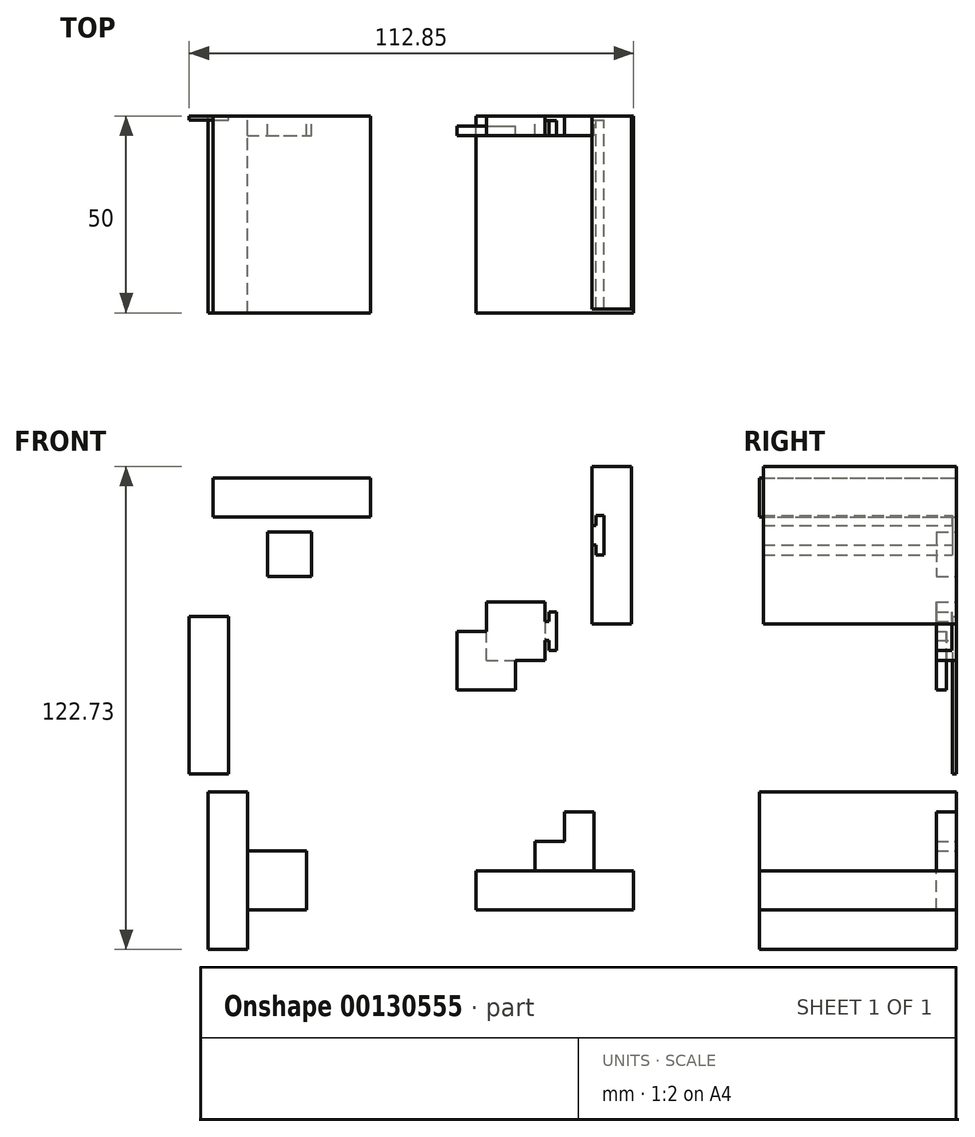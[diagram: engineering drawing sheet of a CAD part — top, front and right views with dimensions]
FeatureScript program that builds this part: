
annotation { "Feature Type Name" : "Feature", "Feature Type Description" : "" }
export const myFeature = defineFeature(function(context is Context, id is Id, definition is map)
    precondition{}
    {
        {
            var Q0;
            Q0=qCreatedBy(makeId("Front.planeOp"),FACE);
            var sketch = newSketch(context, id + "F0", { "sketchPlane" : qUnion([Q0])});
            skLineSegment(sketch, "E0", {"start": v(-53.3, -18.29) * mm, "end": v(-53.3, -58.29) * mm});
            skLineSegment(sketch, "E1", {"start": v(-53.3, -58.29) * mm, "end": v(-43.3, -58.29) * mm});
            skLineSegment(sketch, "E2", {"start": v(-43.3, -58.29) * mm, "end": v(-43.3, -48.29) * mm});
            skLineSegment(sketch, "E3", {"start": v(-43.3, -48.29) * mm, "end": v(-53.3, -48.29) * mm});
            skLineSegment(sketch, "E4", {"start": v(-43.3, -48.29) * mm, "end": v(-43.3, -18.29) * mm});
            skLineSegment(sketch, "E5", {"start": v(-53.3, -18.29) * mm, "end": v(-43.3, -18.29) * mm});
            skLineSegment(sketch, "E6", {"start": v(14.75, -48.29) * mm, "end": v(54.75, -48.29) * mm});
            skLineSegment(sketch, "E7", {"start": v(54.75, -48.29) * mm, "end": v(54.75, -38.29) * mm});
            skLineSegment(sketch, "E8", {"start": v(54.75, -38.29) * mm, "end": v(44.75, -38.29) * mm});
            skLineSegment(sketch, "E9", {"start": v(44.75, -38.29) * mm, "end": v(44.75, -48.29) * mm});
            skLineSegment(sketch, "E10", {"start": v(44.75, -38.29) * mm, "end": v(14.75, -38.29) * mm});
            skLineSegment(sketch, "E11", {"start": v(14.75, -38.29) * mm, "end": v(14.75, -48.29) * mm});
            skLineSegment(sketch, "E12", {"start": v(54.25, 64.44) * mm, "end": v(54.25, 24.44) * mm});
            skLineSegment(sketch, "E13", {"start": v(54.25, 64.44) * mm, "end": v(44.25, 64.44) * mm});
            skLineSegment(sketch, "E14", {"start": v(44.25, 64.44) * mm, "end": v(44.25, 54.44) * mm});
            skLineSegment(sketch, "E15", {"start": v(44.25, 54.44) * mm, "end": v(54.25, 54.44) * mm});
            skLineSegment(sketch, "E16", {"start": v(44.25, 24.44) * mm, "end": v(54.25, 24.44) * mm});
            skLineSegment(sketch, "E17", {"start": v(-52, 61.52) * mm, "end": v(-12, 61.52) * mm});
            skLineSegment(sketch, "E18", {"start": v(-52, 61.52) * mm, "end": v(-52, 51.52) * mm});
            skLineSegment(sketch, "E19", {"start": v(-52, 51.52) * mm, "end": v(-42, 51.52) * mm});
            skLineSegment(sketch, "E20", {"start": v(-42, 51.52) * mm, "end": v(-42, 61.52) * mm});
            skLineSegment(sketch, "E21", {"start": v(-42, 51.52) * mm, "end": v(-12, 51.52) * mm});
            skLineSegment(sketch, "E22", {"start": v(-12, 51.52) * mm, "end": v(-12, 61.52) * mm});
            skLineSegment(sketch, "E23", {"start": v(-42, 51.52) * mm, "end": v(-27, 51.52) * mm});
            skLineSegment(sketch, "E24", {"start": v(-43.3, -48.29) * mm, "end": v(-28.3, -48.29) * mm});
            skLineSegment(sketch, "E25", {"start": v(-28.3, -48.29) * mm, "end": v(-28.3, -33.29) * mm});
            skLineSegment(sketch, "E26", {"start": v(-28.3, -33.29) * mm, "end": v(-43.3, -33.29) * mm});
            skLineSegment(sketch, "E27", {"start": v(-42, 51.52) * mm, "end": v(-42, 36.52) * mm});
            skLineSegment(sketch, "E28", {"start": v(-42, 36.52) * mm, "end": v(-27, 36.52) * mm});
            skLineSegment(sketch, "E29", {"start": v(-27, 51.52) * mm, "end": v(-27, 36.52) * mm});
            skLineSegment(sketch, "E30", {"start": v(-27, 36.52) * mm, "end": v(-38.25, 36.52) * mm});
            skLineSegment(sketch, "E31", {"start": v(-38.25, 36.52) * mm, "end": v(-38.25, 47.77) * mm});
            skLineSegment(sketch, "E32", {"start": v(-38.25, 47.77) * mm, "end": v(-27, 47.77) * mm});
            skLineSegment(sketch, "E33", {"start": v(-34.5, 36.52) * mm, "end": v(-34.5, 44.02) * mm});
            skLineSegment(sketch, "E34", {"start": v(-34.5, 44.02) * mm, "end": v(-27, 44.02) * mm});
            skLineSegment(sketch, "E35", {"start": v(-34.5, 44.02) * mm, "end": v(-27, 47.77) * mm});
            skLineSegment(sketch, "E36", {"start": v(-35.8, -33.29) * mm, "end": v(-35.8, -40.79) * mm});
            skLineSegment(sketch, "E37", {"start": v(-35.8, -40.79) * mm, "end": v(-28.3, -40.79) * mm});
            skLineSegment(sketch, "E38", {"start": v(44.75, -38.29) * mm, "end": v(44.75, -23.29) * mm});
            skLineSegment(sketch, "E39", {"start": v(44.75, -23.29) * mm, "end": v(29.75, -23.29) * mm});
            skLineSegment(sketch, "E40", {"start": v(29.75, -23.29) * mm, "end": v(29.75, -38.29) * mm});
            skLineSegment(sketch, "E41", {"start": v(37.25, -23.29) * mm, "end": v(37.25, -30.79) * mm});
            skLineSegment(sketch, "E42", {"start": v(37.25, -30.79) * mm, "end": v(29.75, -30.79) * mm});
            skLineSegment(sketch, "E43", {"start": v(37.25, -23.29) * mm, "end": v(44.75, -23.29) * mm});
            skLineSegment(sketch, "E44", {"start": v(41, -23.29) * mm, "end": v(41, -34.54) * mm});
            skLineSegment(sketch, "E45", {"start": v(41, -34.54) * mm, "end": v(29.75, -34.54) * mm});
            skLineSegment(sketch, "E46", {"start": v(37.25, -30.79) * mm, "end": v(41, -23.29) * mm});
            skLineSegment(sketch, "E47", {"start": v(44.25, 39.44) * mm, "end": v(44.25, 24.44) * mm});
            skLineSegment(sketch, "E48", {"start": v(44.25, 39.44) * mm, "end": v(44.25, 44.44) * mm});
            skLineSegment(sketch, "E49", {"start": v(44.25, 54.44) * mm, "end": v(44.25, 49.44) * mm});
            skLineSegment(sketch, "E50", {"start": v(44.25, 49.44) * mm, "end": v(45.25, 49.44) * mm});
            skLineSegment(sketch, "E51", {"start": v(44.25, 44.44) * mm, "end": v(45.25, 44.44) * mm});
            skLineSegment(sketch, "E52", {"start": v(45.25, 44.44) * mm, "end": v(45.25, 41.94) * mm});
            skPoint(sketch, "E52.endSnap0", {"position": v(44.25, 41.94) * mm});
            skLineSegment(sketch, "E53", {"start": v(45.25, 49.44) * mm, "end": v(45.25, 51.94) * mm});
            skPoint(sketch, "E53.endSnap0", {"position": v(44.25, 51.94) * mm});
            skLineSegment(sketch, "E54", {"start": v(45.25, 51.94) * mm, "end": v(47.25, 51.94) * mm});
            skLineSegment(sketch, "E55", {"start": v(45.25, 41.94) * mm, "end": v(47.25, 41.94) * mm});
            skLineSegment(sketch, "E56", {"start": v(47.25, 51.94) * mm, "end": v(47.25, 41.94) * mm});
            skLineSegment(sketch, "E57", {"start": v(9.93, 22.55) * mm, "end": v(9.93, 7.65) * mm});
            skLineSegment(sketch, "E58", {"start": v(9.93, 7.65) * mm, "end": v(24.83, 7.65) * mm});
            skLineSegment(sketch, "E59", {"start": v(24.83, 7.65) * mm, "end": v(24.83, 22.55) * mm});
            skLineSegment(sketch, "E60", {"start": v(9.93, 22.55) * mm, "end": v(24.83, 22.55) * mm});
            skPoint(sketch, "E61.endSnap0", {"position": v(17.38, 22.55) * mm});
            skLineSegment(sketch, "E62", {"start": v(17.38, 15.15) * mm, "end": v(32.28, 15.15) * mm});
            skLineSegment(sketch, "E63", {"start": v(17.38, 15.15) * mm, "end": v(17.38, 30.05) * mm});
            skLineSegment(sketch, "E64", {"start": v(17.38, 30.05) * mm, "end": v(32.28, 30.05) * mm});
            skLineSegment(sketch, "E65", {"start": v(44.25, 49.44) * mm, "end": v(44.25, 44.44) * mm});
            skLineSegment(sketch, "E66", {"start": v(32.28, 15.15) * mm, "end": v(32.28, 20.15) * mm});
            skLineSegment(sketch, "E67", {"start": v(32.28, 30.05) * mm, "end": v(32.28, 25.05) * mm});
            skLineSegment(sketch, "E68", {"start": v(32.28, 25.05) * mm, "end": v(33.28, 25.05) * mm});
            skLineSegment(sketch, "E69", {"start": v(33.28, 25.05) * mm, "end": v(33.28, 27.5) * mm});
            skLineSegment(sketch, "E70", {"start": v(33.28, 27.5) * mm, "end": v(35.18, 27.5) * mm});
            skLineSegment(sketch, "E71", {"start": v(32.28, 20.15) * mm, "end": v(33.28, 20.15) * mm});
            skLineSegment(sketch, "E72", {"start": v(33.28, 20.15) * mm, "end": v(33.28, 17.7) * mm});
            skLineSegment(sketch, "E73", {"start": v(33.28, 17.7) * mm, "end": v(35.18, 17.7) * mm});
            skLineSegment(sketch, "E74", {"start": v(35.18, 27.5) * mm, "end": v(35.18, 17.7) * mm});
            skLineSegment(sketch, "E75", {"start": v(32.28, 25.05) * mm, "end": v(32.28, 20.15) * mm});
            skLineSegment(sketch, "E76.bottom", {"start": v(-58.1, 26.35) * mm, "end": v(-48.1, 26.35) * mm});
            skLineSegment(sketch, "E76.top", {"start": v(-58.1, -13.65) * mm, "end": v(-48.1, -13.65) * mm});
            skLineSegment(sketch, "E76.left", {"start": v(-58.1, 26.35) * mm, "end": v(-58.1, -13.65) * mm});
            skLineSegment(sketch, "E76.right", {"start": v(-48.1, 26.35) * mm, "end": v(-48.1, -13.65) * mm});
            skSolve(sketch);
        }
        {
            var Q0;
            {var subQ0=sQuery(id+"F0.wireOp",EDGE,"E1");Q0=makeQuery(id+"F0.imprint","IMPRINT",FACE,{"disambiguationData":[TD([[makeQuery(id+"F0.imprint","IMPRINT",EDGE,{"derivedFrom":subQ0}),1.0]])]});}
            var Q1;
            {var subQ0=sQuery(id+"F0.wireOp",EDGE,"E7");Q1=makeQuery(id+"F0.imprint","IMPRINT",FACE,{"disambiguationData":[TD([[makeQuery(id+"F0.imprint","IMPRINT",EDGE,{"derivedFrom":subQ0}),1.0]])]});}
            var Q2;
            {var subQ0=sQuery(id+"F0.wireOp",EDGE,"E13");Q2=makeQuery(id+"F0.imprint","IMPRINT",FACE,{"disambiguationData":[TD([[makeQuery(id+"F0.imprint","IMPRINT",EDGE,{"derivedFrom":subQ0}),1.0]])]});}
            var Q3;
            {var subQ0=sQuery(id+"F0.wireOp",EDGE,"E18");Q3=makeQuery(id+"F0.imprint","IMPRINT",FACE,{"disambiguationData":[TD([[makeQuery(id+"F0.imprint","IMPRINT",EDGE,{"derivedFrom":subQ0}),1.0]])]});}
            var Q4;
            {var subQ4=sQuery(id+"F0.wireOp",EDGE,"E36");Q4=makeQuery(id+"F0.imprint","IMPRINT",FACE,{"disambiguationData":[TD([[makeQuery(id+"F0.imprint","IMPRINT",EDGE,{"derivedFrom":subQ4}),1.0]])]});}
            var Q5;
            Q5=makeQuery(id+"F0.imprint","IMPRINT",FACE,{"disambiguationData":[TD([[makeQuery(id+"F0.imprint","IMPRINT",EDGE,{"derivedFrom":sQuery(id+"F0.wireOp",EDGE,"E50")}),-1.0]])]});
            var Q6;
            {var subQ1=sQuery(id+"F0.wireOp",EDGE,"E57");Q6=makeQuery(id+"F0.imprint","IMPRINT",FACE,{"disambiguationData":[TD([[makeQuery(id+"F0.imprint","IMPRINT",EDGE,{"derivedFrom":subQ1}),1.0]])]});}
            var Q7;
            Q7=makeQuery(id+"F0.imprint","IMPRINT",FACE,{"disambiguationData":[TD([[makeQuery(id+"F0.imprint","IMPRINT",EDGE,{"derivedFrom":sQuery(id+"F0.wireOp",EDGE,"E68")}),-1.0]])]});
            var Q8;
            {var subQ3=sQuery(id+"F0.wireOp",EDGE,"E3");Q8=makeQuery(id+"F0.imprint","IMPRINT",FACE,{"disambiguationData":[TD([[makeQuery(id+"F0.imprint","IMPRINT",EDGE,{"derivedFrom":subQ3}),-1.0]])]});}
            var Q9;
            {var subQ1=sQuery(id+"F0.wireOp",EDGE,"E24");Q9=makeQuery(id+"F0.imprint","IMPRINT",FACE,{"disambiguationData":[TD([[makeQuery(id+"F0.imprint","IMPRINT",EDGE,{"derivedFrom":subQ1}),1.0]])]});}
            var Q10;
            {var subQ3=sQuery(id+"F0.wireOp",EDGE,"E9");Q10=makeQuery(id+"F0.imprint","IMPRINT",FACE,{"disambiguationData":[TD([[makeQuery(id+"F0.imprint","IMPRINT",EDGE,{"derivedFrom":subQ3}),-1.0]])]});}
            var Q11;
            {var subQ4=sQuery(id+"F0.wireOp",EDGE,"E38");Q11=makeQuery(id+"F0.imprint","IMPRINT",FACE,{"disambiguationData":[TD([[makeQuery(id+"F0.imprint","IMPRINT",EDGE,{"derivedFrom":subQ4}),1.0]])]});}
            var Q12;
            {var subQ2=sQuery(id+"F0.wireOp",EDGE,"E15");Q12=makeQuery(id+"F0.imprint","IMPRINT",FACE,{"disambiguationData":[TD([[makeQuery(id+"F0.imprint","IMPRINT",EDGE,{"derivedFrom":subQ2}),-1.0]])]});}
            var Q13;
            {var subQ1=sQuery(id+"F0.wireOp",EDGE,"E20");Q13=makeQuery(id+"F0.imprint","IMPRINT",FACE,{"disambiguationData":[TD([[makeQuery(id+"F0.imprint","IMPRINT",EDGE,{"derivedFrom":subQ1}),-1.0]])]});}
            var Q14;
            {var subQ1=sQuery(id+"F0.wireOp",EDGE,"E23");Q14=makeQuery(id+"F0.imprint","IMPRINT",FACE,{"disambiguationData":[TD([[makeQuery(id+"F0.imprint","IMPRINT",EDGE,{"derivedFrom":subQ1}),-1.0]])]});}
            var Q15;
            {var subQ2=sQuery(id+"F0.wireOp",EDGE,"E34");Q15=makeQuery(id+"F0.imprint","IMPRINT",FACE,{"disambiguationData":[TD([[makeQuery(id+"F0.imprint","IMPRINT",EDGE,{"derivedFrom":subQ2}),1.0]])]});}
            var Q16;
            {var subQ4=sQuery(id+"F0.wireOp",EDGE,"E33");Q16=makeQuery(id+"F0.imprint","IMPRINT",FACE,{"disambiguationData":[TD([[makeQuery(id+"F0.imprint","IMPRINT",EDGE,{"derivedFrom":subQ4}),-1.0]])]});}
            var Q17;
            {var subQ0=sQuery(id+"F0.wireOp",EDGE,"E39");Q17=makeQuery(id+"F0.imprint","IMPRINT",FACE,{"disambiguationData":[TD([[makeQuery(id+"F0.imprint","IMPRINT",EDGE,{"derivedFrom":subQ0}),1.0]])]});}
            var Q18;
            {var subQ0=sQuery(id+"F0.wireOp",EDGE,"E41");Q18=makeQuery(id+"F0.imprint","IMPRINT",FACE,{"disambiguationData":[TD([[makeQuery(id+"F0.imprint","IMPRINT",EDGE,{"derivedFrom":subQ0}),1.0]])]});}
            var Q19;
            {var subQ0=sQuery(id+"F0.wireOp",EDGE,"E60");var subQ1=sQuery(id+"F0.wireOp",EDGE,"E59");var subQ2=makeQuery(id+"F0.imprint","INTERSECT",VERTEX,{"derivedFrom":[subQ1,subQ0]});Q19=makeQuery(id+"F0.imprint","IMPRINT",FACE,{"disambiguationData":[TD([[makeQuery(id+"F0.imprint","IMPRINT",EDGE,{"disambiguationData":[TD([[subQ2,1.0]])],"derivedFrom":subQ1}),1.0]])]});}
            var Q20;
            {var subQ0=sQuery(id+"F0.wireOp",EDGE,"E64");Q20=makeQuery(id+"F0.imprint","IMPRINT",FACE,{"disambiguationData":[TD([[makeQuery(id+"F0.imprint","IMPRINT",EDGE,{"derivedFrom":subQ0}),-1.0]])]});}
            var Q21;
            {var subQ1=sQuery(id+"F0.wireOp",EDGE,"E31");Q21=makeQuery(id+"F0.imprint","IMPRINT",FACE,{"disambiguationData":[TD([[makeQuery(id+"F0.imprint","IMPRINT",EDGE,{"derivedFrom":subQ1}),-1.0]])]});}
            var Q22;
            {var subQ1=sQuery(id+"F0.wireOp",EDGE,"E42");Q22=makeQuery(id+"F0.imprint","IMPRINT",FACE,{"disambiguationData":[TD([[makeQuery(id+"F0.imprint","IMPRINT",EDGE,{"derivedFrom":subQ1}),1.0]])]});}
            extrude(context, id + "F1", {"entities" : qUnion([Q0, Q1, Q2, Q3, Q4, Q5, Q6, Q7, Q8, Q9, Q10, Q11, Q12, Q13, Q14, Q15, Q16, Q17, Q18, Q19, Q20, Q21, Q22]), "depth" : 5 * mm});
        }
        {
            var Q0;
            Q0=makeQuery(id+"F1.opExtrude","CAP_FACE",FACE,{"disambiguationData":[OSD([sQuery(id+"F0.wireOp",EDGE,"E17"),sQuery(id+"F0.wireOp",EDGE,"E18"),sQuery(id+"F0.wireOp",EDGE,"E19"),sQuery(id+"F0.wireOp",EDGE,"E21"),sQuery(id+"F0.wireOp",EDGE,"E22"),sQuery(id+"F0.wireOp",EDGE,"E27"),sQuery(id+"F0.wireOp",EDGE,"E28"),sQuery(id+"F0.wireOp",EDGE,"E29"),sQuery(id+"F0.wireOp",EDGE,"E30")])],"isStart":false});
            var sketch = newSketch(context, id + "F2", { "sketchPlane" : qUnion([Q0])});
            skLineSegment(sketch, "E77.0", {"start": v(-42, 51.52) * mm, "end": v(-42, 61.52) * mm});
            skLineSegment(sketch, "E78.0", {"start": v(-42, 51.52) * mm, "end": v(-27, 51.52) * mm});
            skLineSegment(sketch, "E79.0", {"start": v(-38.25, 47.77) * mm, "end": v(-27, 47.77) * mm});
            skLineSegment(sketch, "E80.0", {"start": v(-38.25, 36.52) * mm, "end": v(-38.25, 47.77) * mm});
            skLineSegment(sketch, "E81.0", {"start": v(-34.5, 44.02) * mm, "end": v(-27, 47.77) * mm});
            skLineSegment(sketch, "E82.0", {"start": v(-34.5, 44.02) * mm, "end": v(-27, 44.02) * mm});
            skLineSegment(sketch, "E83.0", {"start": v(-34.5, 36.52) * mm, "end": v(-34.5, 44.02) * mm});
            skLineSegment(sketch, "E84.0", {"start": v(44.25, 54.44) * mm, "end": v(54.25, 54.44) * mm});
            skLineSegment(sketch, "E85.0", {"start": v(47.25, 51.94) * mm, "end": v(47.25, 41.94) * mm});
            skLineSegment(sketch, "E86.0", {"start": v(45.25, 51.94) * mm, "end": v(47.25, 51.94) * mm});
            skLineSegment(sketch, "E87.0", {"start": v(45.25, 41.94) * mm, "end": v(47.25, 41.94) * mm});
            skLineSegment(sketch, "E88.0", {"start": v(45.25, 44.44) * mm, "end": v(45.25, 41.94) * mm});
            skLineSegment(sketch, "E89.0", {"start": v(44.25, 44.44) * mm, "end": v(45.25, 44.44) * mm});
            skLineSegment(sketch, "E90.0", {"start": v(44.25, 49.44) * mm, "end": v(45.25, 49.44) * mm});
            skLineSegment(sketch, "E91.0", {"start": v(45.25, 49.44) * mm, "end": v(45.25, 51.94) * mm});
            skLineSegment(sketch, "E92.0", {"start": v(32.28, 25.05) * mm, "end": v(32.28, 20.15) * mm});
            skLineSegment(sketch, "E93.0", {"start": v(9.93, 22.55) * mm, "end": v(24.83, 22.55) * mm});
            skLineSegment(sketch, "E94.0", {"start": v(24.83, 7.65) * mm, "end": v(24.83, 22.55) * mm});
            skLineSegment(sketch, "E95.0", {"start": v(17.38, 15.15) * mm, "end": v(32.28, 15.15) * mm});
            skLineSegment(sketch, "E96.0", {"start": v(17.38, 15.15) * mm, "end": v(17.38, 30.05) * mm});
            skLineSegment(sketch, "E97.0", {"start": v(-43.3, -48.29) * mm, "end": v(-43.3, -18.29) * mm});
            skLineSegment(sketch, "E98.0", {"start": v(-43.3, -48.29) * mm, "end": v(-53.3, -48.29) * mm});
            skLineSegment(sketch, "E99.0", {"start": v(-35.8, -33.29) * mm, "end": v(-35.8, -40.79) * mm});
            skLineSegment(sketch, "E100.0", {"start": v(-35.8, -40.79) * mm, "end": v(-28.3, -40.79) * mm});
            skLineSegment(sketch, "E101.0", {"start": v(37.25, -23.29) * mm, "end": v(37.25, -30.79) * mm});
            skLineSegment(sketch, "E102.0", {"start": v(37.25, -30.79) * mm, "end": v(29.75, -30.79) * mm});
            skLineSegment(sketch, "E103.0", {"start": v(37.25, -30.79) * mm, "end": v(41, -23.29) * mm});
            skLineSegment(sketch, "E104.0", {"start": v(41, -23.29) * mm, "end": v(41, -34.54) * mm});
            skLineSegment(sketch, "E105.0", {"start": v(41, -34.54) * mm, "end": v(29.75, -34.54) * mm});
            skLineSegment(sketch, "E106.0", {"start": v(44.75, -38.29) * mm, "end": v(14.75, -38.29) * mm});
            skLineSegment(sketch, "E107.0", {"start": v(44.75, -38.29) * mm, "end": v(44.75, -48.29) * mm});
            skSolve(sketch);
        }
        {
            var Q0;
            {var subQ0=sQuery(id+"F2.wireOp",EDGE,"E77.0");Q0=makeQuery(id+"F2.imprint","IMPRINT",FACE,{"disambiguationData":[TD([[makeQuery(id+"F2.imprint","IMPRINT",EDGE,{"derivedFrom":subQ0}),1.0]])]});}
            var Q1;
            {var subQ1=sQuery(id+"F2.wireOp",EDGE,"E77.0");Q1=makeQuery(id+"F2.imprint","IMPRINT",FACE,{"disambiguationData":[TD([[makeQuery(id+"F2.imprint","IMPRINT",EDGE,{"derivedFrom":subQ1}),-1.0]])]});}
            extrude(context, id + "F3", {"entities" : qUnion([Q0, Q1]), "operationType" : NewBodyOperationType.ADD, "depth" : 45 * mm});
        }
        {
            var Q0;
            Q0=makeQuery(id+"F1.opExtrude","CAP_FACE",FACE,{"disambiguationData":[OSD([sQuery(id+"F0.wireOp",EDGE,"E0"),sQuery(id+"F0.wireOp",EDGE,"E1"),sQuery(id+"F0.wireOp",EDGE,"E2"),sQuery(id+"F0.wireOp",EDGE,"E4"),sQuery(id+"F0.wireOp",EDGE,"E5"),sQuery(id+"F0.wireOp",EDGE,"E24"),sQuery(id+"F0.wireOp",EDGE,"E25"),sQuery(id+"F0.wireOp",EDGE,"E26")])],"isStart":false});
            var sketch = newSketch(context, id + "F4", { "sketchPlane" : qUnion([Q0])});
            skLineSegment(sketch, "E108.0", {"start": v(-43.3, -48.29) * mm, "end": v(-53.3, -48.29) * mm});
            skLineSegment(sketch, "E109.0", {"start": v(-43.3, -48.29) * mm, "end": v(-43.3, -18.29) * mm});
            skLineSegment(sketch, "E110.0", {"start": v(-35.8, -33.29) * mm, "end": v(-35.8, -40.79) * mm});
            skLineSegment(sketch, "E111.0", {"start": v(-35.8, -40.79) * mm, "end": v(-28.3, -40.79) * mm});
            skSolve(sketch);
        }
        {
            var Q0;
            {var subQ0=sQuery(id+"F4.wireOp",EDGE,"E108.0");Q0=makeQuery(id+"F4.imprint","IMPRINT",FACE,{"disambiguationData":[TD([[makeQuery(id+"F4.imprint","IMPRINT",EDGE,{"derivedFrom":subQ0}),1.0]])]});}
            var Q1;
            {var subQ2=sQuery(id+"F4.wireOp",EDGE,"E108.0");Q1=makeQuery(id+"F4.imprint","IMPRINT",FACE,{"disambiguationData":[TD([[makeQuery(id+"F4.imprint","IMPRINT",EDGE,{"derivedFrom":subQ2}),-1.0]])]});}
            extrude(context, id + "F5", {"entities" : qUnion([Q0, Q1]), "operationType" : NewBodyOperationType.ADD, "depth" : 45 * mm});
        }
        {
            var Q0;
            Q0=makeQuery(id+"F1.opExtrude","CAP_FACE",FACE,{"disambiguationData":[OSD([sQuery(id+"F0.wireOp",EDGE,"E12"),sQuery(id+"F0.wireOp",EDGE,"E13"),sQuery(id+"F0.wireOp",EDGE,"E14"),sQuery(id+"F0.wireOp",EDGE,"E16"),sQuery(id+"F0.wireOp",EDGE,"E47"),sQuery(id+"F0.wireOp",EDGE,"E48"),sQuery(id+"F0.wireOp",EDGE,"E49"),sQuery(id+"F0.wireOp",EDGE,"E65")])],"isStart":false});
            var sketch = newSketch(context, id + "F6", { "sketchPlane" : qUnion([Q0])});
            skLineSegment(sketch, "E112.0", {"start": v(44.25, 54.44) * mm, "end": v(54.25, 54.44) * mm});
            skLineSegment(sketch, "E113.0", {"start": v(44.25, 49.44) * mm, "end": v(45.25, 49.44) * mm});
            skLineSegment(sketch, "E114.0", {"start": v(45.25, 49.44) * mm, "end": v(45.25, 51.94) * mm});
            skLineSegment(sketch, "E115.0", {"start": v(45.25, 51.94) * mm, "end": v(47.25, 51.94) * mm});
            skLineSegment(sketch, "E116.0", {"start": v(47.25, 51.94) * mm, "end": v(47.25, 41.94) * mm});
            skLineSegment(sketch, "E117.0", {"start": v(45.25, 41.94) * mm, "end": v(47.25, 41.94) * mm});
            skLineSegment(sketch, "E118.0", {"start": v(45.25, 44.44) * mm, "end": v(45.25, 41.94) * mm});
            skLineSegment(sketch, "E119.0", {"start": v(44.25, 44.44) * mm, "end": v(45.25, 44.44) * mm});
            skLineSegment(sketch, "E120.0", {"start": v(44.25, 64.44) * mm, "end": v(44.25, 54.44) * mm});
            skLineSegment(sketch, "E121.0", {"start": v(54.25, 64.44) * mm, "end": v(44.25, 64.44) * mm});
            skLineSegment(sketch, "E122.0", {"start": v(54.25, 64.44) * mm, "end": v(54.25, 24.44) * mm});
            skLineSegment(sketch, "E123.0", {"start": v(44.25, 49.44) * mm, "end": v(44.25, 44.44) * mm});
            skLineSegment(sketch, "E124.0", {"start": v(44.25, 39.44) * mm, "end": v(44.25, 44.44) * mm});
            skLineSegment(sketch, "E125.0", {"start": v(44.25, 39.44) * mm, "end": v(44.25, 24.44) * mm});
            skLineSegment(sketch, "E126.0", {"start": v(44.25, 24.44) * mm, "end": v(54.25, 24.44) * mm});
            skLineSegment(sketch, "E127.0", {"start": v(44.25, 54.44) * mm, "end": v(44.25, 49.44) * mm});
            skSolve(sketch);
        }
        {
            var Q0;
            {var subQ0=sQuery(id+"F6.wireOp",EDGE,"E112.0");Q0=makeQuery(id+"F6.imprint","IMPRINT",FACE,{"disambiguationData":[TD([[makeQuery(id+"F6.imprint","IMPRINT",EDGE,{"derivedFrom":subQ0}),1.0]])]});}
            var Q1;
            {var subQ2=sQuery(id+"F6.wireOp",EDGE,"E112.0");Q1=makeQuery(id+"F6.imprint","IMPRINT",FACE,{"disambiguationData":[TD([[makeQuery(id+"F6.imprint","IMPRINT",EDGE,{"derivedFrom":subQ2}),-1.0]])]});}
            extrude(context, id + "F7", {"entities" : qUnion([Q0, Q1]), "operationType" : NewBodyOperationType.ADD, "depth" : 44 * mm});
        }
        {
            var Q0;
            Q0=makeQuery(id+"F0.imprint","IMPRINT",FACE,{"disambiguationData":[TD([[makeQuery(id+"F0.imprint","IMPRINT",EDGE,{"derivedFrom":sQuery(id+"F0.wireOp",EDGE,"E76.bottom")}),-1.0]])]});
            extrude(context, id + "F8", {"entities" : qUnion([Q0]), "depth" : 1 * mm});
        }
        {
            var Q0;
            Q0=makeQuery(id+"F1.opExtrude","CAP_FACE",FACE,{"disambiguationData":[OSD([sQuery(id+"F0.wireOp",EDGE,"E6"),sQuery(id+"F0.wireOp",EDGE,"E7"),sQuery(id+"F0.wireOp",EDGE,"E8"),sQuery(id+"F0.wireOp",EDGE,"E10"),sQuery(id+"F0.wireOp",EDGE,"E11"),sQuery(id+"F0.wireOp",EDGE,"E38"),sQuery(id+"F0.wireOp",EDGE,"E39"),sQuery(id+"F0.wireOp",EDGE,"E40"),sQuery(id+"F0.wireOp",EDGE,"E43")])],"isStart":false});
            var sketch = newSketch(context, id + "F9", { "sketchPlane" : qUnion([Q0])});
            skLineSegment(sketch, "E128.0", {"start": v(44.75, -38.29) * mm, "end": v(14.75, -38.29) * mm});
            skLineSegment(sketch, "E129.0", {"start": v(41, -34.54) * mm, "end": v(29.75, -34.54) * mm});
            skLineSegment(sketch, "E130.0", {"start": v(37.25, -30.79) * mm, "end": v(29.75, -30.79) * mm});
            skLineSegment(sketch, "E131.0", {"start": v(37.25, -23.29) * mm, "end": v(37.25, -30.79) * mm});
            skLineSegment(sketch, "E132.0", {"start": v(37.25, -30.79) * mm, "end": v(41, -23.29) * mm});
            skLineSegment(sketch, "E133.0", {"start": v(41, -23.29) * mm, "end": v(41, -34.54) * mm});
            skLineSegment(sketch, "E134.0", {"start": v(44.75, -38.29) * mm, "end": v(44.75, -48.29) * mm});
            skSolve(sketch);
        }
        {
            var Q0;
            {var subQ0=sQuery(id+"F9.wireOp",EDGE,"E134.0");Q0=makeQuery(id+"F9.imprint","IMPRINT",FACE,{"disambiguationData":[TD([[makeQuery(id+"F9.imprint","IMPRINT",EDGE,{"derivedFrom":subQ0}),1.0]])]});}
            var Q1;
            {var subQ0=sQuery(id+"F9.wireOp",EDGE,"E134.0");Q1=makeQuery(id+"F9.imprint","IMPRINT",FACE,{"disambiguationData":[TD([[makeQuery(id+"F9.imprint","IMPRINT",EDGE,{"derivedFrom":subQ0}),-1.0]])]});}
            extrude(context, id + "F10", {"entities" : qUnion([Q0, Q1]), "operationType" : NewBodyOperationType.ADD, "depth" : 45 * mm});
        }
        {
            var Q0;
            Q0=makeQuery(id+"F1.opExtrude","CAP_FACE",FACE,{"disambiguationData":[OSD([sQuery(id+"F0.wireOp",EDGE,"E12"),sQuery(id+"F0.wireOp",EDGE,"E13"),sQuery(id+"F0.wireOp",EDGE,"E14"),sQuery(id+"F0.wireOp",EDGE,"E16"),sQuery(id+"F0.wireOp",EDGE,"E47"),sQuery(id+"F0.wireOp",EDGE,"E48"),sQuery(id+"F0.wireOp",EDGE,"E49"),sQuery(id+"F0.wireOp",EDGE,"E65")])],"isStart":false});
            extrude(context, id + "F11", {"entities" : qUnion([Q0]), "operationType" : NewBodyOperationType.REMOVE, "oppositeDirection" : true, "depth" : 4 * mm});
        }
        {
            var Q0;
            Q0=makeQuery(id+"F0.imprint","IMPRINT",FACE,{"disambiguationData":[TD([[makeQuery(id+"F0.imprint","IMPRINT",EDGE,{"derivedFrom":sQuery(id+"F0.wireOp",EDGE,"E68")}),-1.0]])]});
            extrude(context, id + "F12", {"entities" : qUnion([Q0]), "operationType" : NewBodyOperationType.REMOVE, "depth" : 1.1 * mm});
        }
        {
            var Q0;
            {var subQ1=sQuery(id+"F0.wireOp",EDGE,"E57");Q0=makeQuery(id+"F0.imprint","IMPRINT",FACE,{"disambiguationData":[TD([[makeQuery(id+"F0.imprint","IMPRINT",EDGE,{"derivedFrom":subQ1}),1.0]])]});}
            extrude(context, id + "F13", {"entities" : qUnion([Q0]), "operationType" : NewBodyOperationType.REMOVE, "depth" : 2.5 * mm});
        }
    });
